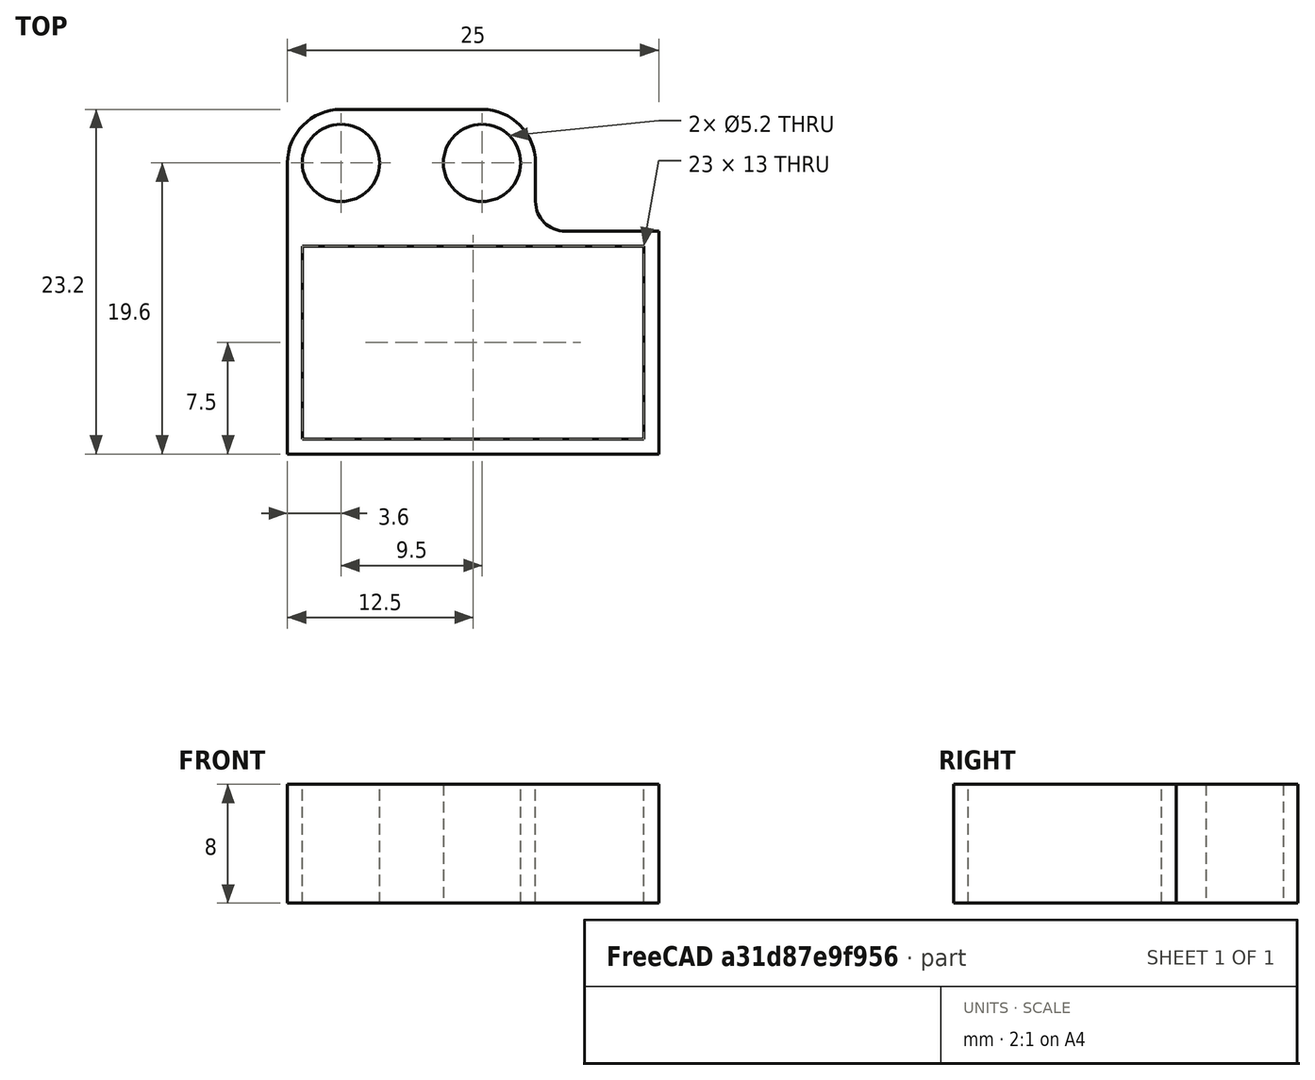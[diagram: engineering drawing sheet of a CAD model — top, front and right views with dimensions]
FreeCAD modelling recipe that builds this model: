
FCSTD DOCUMENT  (FreeCAD 0.18R4 (GitTag))
Label: Servo_Mount
License: All rights reserved
LicenseURL: http://en.wikipedia.org/wiki/All_rights_reserved
objects: Sketcher::SketchObject×1, PartDesign::Pad×1, PartDesign::Body×1, Mesh::Feature×1
note: 4 computed .brp shape members not serialized (recipe doc carries the construction recipe); baked Part::Feature solids carry a one-line shape summary decoded from their .brp

FEATURE [Sketcher::SketchObject] Sketch
  MapMode = 5
  Support = -> [XY_Plane]
  sketch-geometry (16):
    g0: LineSegment StartX=-11.5 StartY=-6.5 StartZ=0 EndX=11.5 EndY=-6.5 EndZ=0
    g1: LineSegment StartX=11.5 StartY=-6.5 StartZ=0 EndX=11.5 EndY=6.5 EndZ=0
    g2: LineSegment StartX=11.5 StartY=6.5 StartZ=0 EndX=-11.5 EndY=6.5 EndZ=0
    g3: LineSegment StartX=-11.5 StartY=6.5 StartZ=0 EndX=-11.5 EndY=-6.5 EndZ=0
    g4: LineSegment StartX=-12.5 StartY=-7.5 StartZ=0 EndX=12.5 EndY=-7.5 EndZ=0
    g5: LineSegment StartX=12.5 StartY=-7.5 StartZ=0 EndX=12.5 EndY=7.5 EndZ=0
    g6: LineSegment StartX=-12.5 StartY=12.1 StartZ=0 EndX=-12.5 EndY=-7.5 EndZ=0
    g7: Circle CenterX=-8.9 CenterY=12.1 CenterZ=0 NormalX=0 NormalY=0 NormalZ=1 AngleXU=0 Radius=2.6
    g8: Circle CenterX=0.6 CenterY=12.1 CenterZ=0 NormalX=0 NormalY=0 NormalZ=1 AngleXU=0 Radius=2.6
    g9: LineSegment [constr] StartX=-8.9 StartY=9.5 StartZ=0 EndX=0.600014 EndY=9.5 EndZ=0
    g10: ArcOfCircle CenterX=-8.9 CenterY=12.1 CenterZ=0 NormalX=0 NormalY=0 NormalZ=1 AngleXU=0 Radius=3.6 StartAngle=1.5708 EndAngle=3.14159
    g11: ArcOfCircle CenterX=0.6 CenterY=12.1 CenterZ=0 NormalX=0 NormalY=0 NormalZ=1 AngleXU=0 Radius=3.6 StartAngle=0 EndAngle=1.5708
    g12: LineSegment StartX=-8.9 StartY=15.7 StartZ=0 EndX=0.6 EndY=15.7 EndZ=0
    g13: ArcOfCircle CenterX=6.2 CenterY=9.5 CenterZ=0 NormalX=0 NormalY=0 NormalZ=1 AngleXU=0 Radius=2 StartAngle=3.14159 EndAngle=4.71239
    g14: LineSegment StartX=12.5 StartY=7.5 StartZ=0 EndX=6.2 EndY=7.5 EndZ=0
    g15: LineSegment StartX=4.2 StartY=12.1 StartZ=0 EndX=4.2 EndY=9.5 EndZ=0
  constraints (40):
    c: Coincident(g0,g1)
    c: Coincident(g1,g2)
    c: Coincident(g2,g3)
    c: Coincident(g3,g0)
    c: Horizontal(g2)
    c: Vertical(g1)
    c: Coincident(g4,g5)
    c: Coincident(g6,g4)
    c: DistanceY(g1,g1) = 13
    c: DistanceX(g2,g2) = 23
    c: Symmetric(g0,g0,g-2)
    c: Symmetric(g0,g2,g-1)
    c: Symmetric(g4,g4,g-2)
    c: DistanceX(g0,g4) = 1
    c: DistanceY(g4,g0) = 1
    c: Equal(g8,g7)
    c: Radius(g8) = 2.6
    c: DistanceX(g7,g8) = 9.5
    c: PointOnObject(g9,g7)
    c: Horizontal(g9)
    c: PointOnObject(g9,g8)
    c: Tangent(g9,g7,g9) = -1.5708
    c: DistanceY(g1,g9) = 3
    c: Coincident(g10,g7)
    c: Radius(g10) = 3.6
    c: Coincident(g11,g8)
    c: Horizontal(g12)
    c: Tangent(g12,g11) = 1.5708
    c: Vertical(g6)
    c: Tangent(g10,g6) = -1.5708
    c: Tangent(g12,g10) = 1.5708
    c: Horizontal(g7,g8)
    c: Coincident(g14,g5)
    c: Horizontal(g14)
    c: Tangent(g14,g13) = 1.5708
    c: Symmetric(g5,g4,g-1)
    c: Radius(g13) = 2
    c: Tangent(g15,g11) = 1.5708
    c: Tangent(g15,g13) = -1.5708
    c: Vertical(g15)
FEATURE [PartDesign::Pad] Pad
  Length = 8
  Length2 = 100
  Profile = -> Sketch
  Refine = true
  Type = 0
FEATURE [PartDesign::Body] Body
  Group = -> [Sketch,Pad]
  Origin = -> Origin
  Tip = -> Pad
FEATURE [Mesh::Feature] Mesh  label="Pad (Meshed)"
